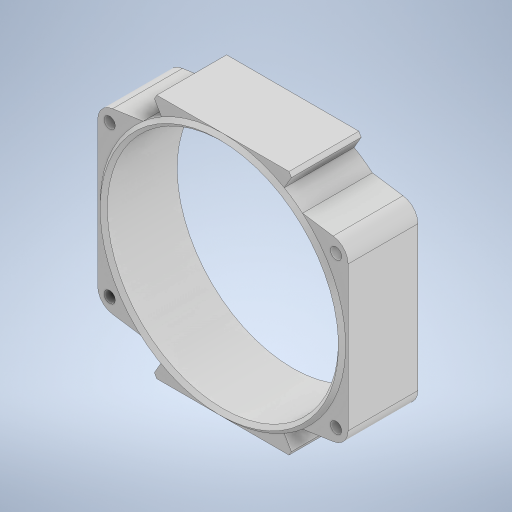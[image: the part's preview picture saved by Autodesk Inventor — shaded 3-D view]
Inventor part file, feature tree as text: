
AUTODESK INVENTOR PART (.ipt)
format: ipt  version: 2023.4 (Build 274418000, 418)  size: 497,664 bytes
history: native  units: mm
features: extrude x17, sketch x7, chamfer x3, projected_geometry x3, mirror x1
ambient origin geometry x8: Origin, YZ Plane, XZ Plane, XY Plane, X Axis, Y Axis, Z Axis, Center Point
bodies: Solid1 (feature_tree)
feature tree (31):
  extrude  "Extrusion1"  Depth=102.0mm
  extrude  "Extrusion2"  Depth=1.5mm TaperAngle=45.0deg
  chamfer  "Chamfer1"  Distance=1.5mm
  extrude  "Extrusion3"  Depth=4.7mm
  extrude  "Extrusion4"  Depth=4.7mm
  extrude  "Extrusion5"  Depth=10.1mm TaperAngle=0.0deg
  extrude  "Extrusion6"  Depth=14.0mm TaperAngle=0.0deg
  extrude  "Extrusion7"  Depth=10.0mm
  chamfer  "Chamfer2"  Distance=7.0mm
  extrude  "Extrusion8"  Depth=10.0mm
  extrude  "Extrusion11"  Depth=10.0mm TaperAngle=0.0deg
  extrude  "Extrusion12"  Depth=10.0mm TaperAngle=0.0deg
  extrude  "Extrusion13"  Depth=29.0mm
  extrude  "Extrusion14"  Depth=15.0mm TaperAngle=0.0deg
  extrude  "Extrusion17"  Depth=10.0mm TaperAngle=0.0deg
  extrude  "Extrusion18"  Depth=10.0mm TaperAngle=0.0deg
  extrude  "Extrusion19"  Depth=10.0mm
  extrude  "Extrusion20"  Depth=10.0mm
  mirror  "Mirror1"
  extrude  "Extrusion21"  Depth=15.0mm TaperAngle=0.0deg
  chamfer  "Chamfer4"  Distance=15.0mm
  sketch  "Sketch1"  dims[d0=29.0mm d1=0.0mm d2=102.0mm]
  sketch  "Sketch4"  dims[d3=1.5mm d4=0.0mm d5=1.5mm d6=2.0mm d7=45.0deg d9=1.5mm d10=0.0mm]
  sketch  "Sketch7"  dims[d11=0.0mm d12=0.0mm d13=4.7mm]
  sketch  "Sketch11"  dims[d14=4.7mm d15=4.7mm]
  projected_geometry  "Projected Loop1"
  sketch  "Sketch23"  dims[d16=4.7mm d17=10.1mm d18=0.0mm]
  projected_geometry  "Projected Loop5"
  sketch  "Sketch24"  dims[d19=15.0mm d20=0.0mm d21=14.0mm d22=0.0mm]
  sketch  "Sketch25"  dims[d23=2.6mm d24=2.0mm d25=45.0deg d26=5.75mm d27=7.0mm d35=14.5mm d36=20.0mm d37=0.0mm d55=2.0mm d56=0.0mm d60=29.0mm d61=15.0mm d62=0.0mm d63=20.0mm d64=0.0mm d65=10.0mm d66=0.0mm d83=5.75mm d84=5.75mm d85=15.0mm d86=0.0mm d87=15.0mm d88=0.0mm d94=10.0mm d95=0.0mm d96=0.0mm d97=0.0mm d98=30.0deg d99=30.0deg d100=10.0mm d101=0.0mm d102=2.0mm d103=2.0mm d104=45.0deg]
  projected_geometry  "Projected Loop6"
